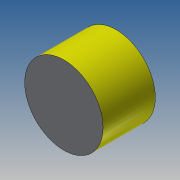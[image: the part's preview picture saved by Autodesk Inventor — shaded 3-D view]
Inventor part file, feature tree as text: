
AUTODESK INVENTOR PART (.ipt)
format: ipt  version: 2015 (Build 190159000, 159)  size: 90,624 bytes
history: native  units: mm
features: revolve x1, sketch x1
ambient origin geometry x8: Origin, YZ Plane, XZ Plane, XY Plane, X Axis, Y Axis, Z Axis, Center Point
bodies: Solid1 (feature_tree)
feature tree (2):
  revolve  "Revolution1"  [1 undecoded]
  sketch  "Sketch1"  dims[d0=300.0mm d1=200.0mm d2=5.0mm d3=20.0mm d4=90.0deg]
note: 1 required parameter value undecoded (feature->parameter linkage not recoverable at this tier; creation-order binding heuristic only, values carry confidence <= 0.55)
